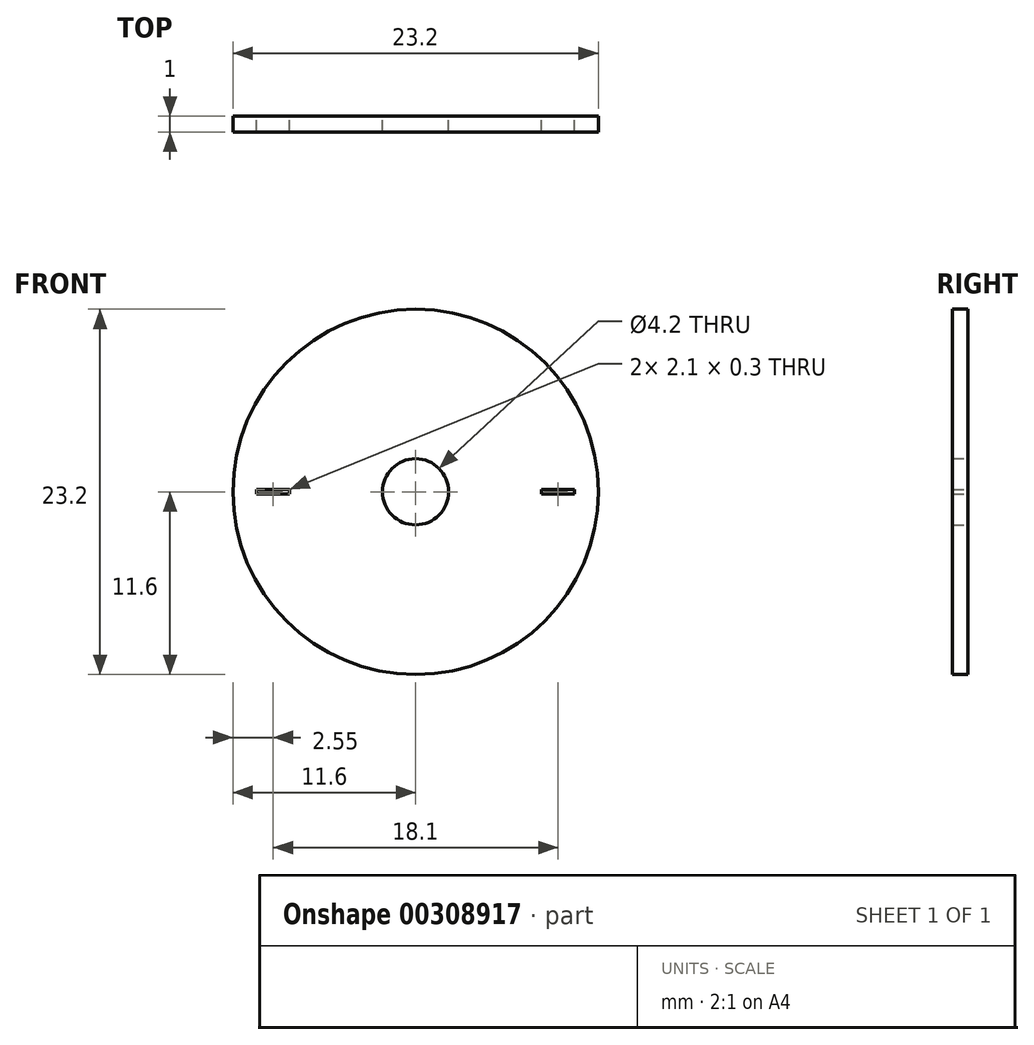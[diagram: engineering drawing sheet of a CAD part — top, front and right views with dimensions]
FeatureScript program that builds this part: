
annotation { "Feature Type Name" : "Feature", "Feature Type Description" : "" }
export const myFeature = defineFeature(function(context is Context, id is Id, definition is map)
    precondition{}
    {
        {
            var Q0;
            Q0=qCreatedBy(makeId("Front.planeOp"),FACE);
            var sketch = newSketch(context, id + "F0", { "sketchPlane" : qUnion([Q0])});
            skCircle(sketch, "E0", {"center": v(0, 0) * mm, "radius": 11.6 * mm});
            skCircle(sketch, "E1", {"center": v(0, 0) * mm, "radius": 2.1 * mm});
            skLineSegment(sketch, "E2.bottom", {"start": v(-10.1, 0.15) * mm, "end": v(-8, 0.15) * mm});
            skLineSegment(sketch, "E2.top", {"start": v(-10.1, -0.15) * mm, "end": v(-8, -0.15) * mm});
            skLineSegment(sketch, "E2.left", {"start": v(-10.1, 0.15) * mm, "end": v(-10.1, -0.15) * mm});
            skLineSegment(sketch, "E2.right", {"start": v(-8, 0.15) * mm, "end": v(-8, -0.15) * mm});
            skLineSegment(sketch, "E3", {"start": v(-9.05, 0.15) * mm, "end": v(-9.05, -0.15) * mm, "construction": true});
            skLineSegment(sketch, "E4.MirrorCS", {"start": v(8, 0.15) * mm, "end": v(8, -0.15) * mm});
            skLineSegment(sketch, "E5.MirrorCS", {"start": v(10.1, 0.15) * mm, "end": v(8, 0.15) * mm});
            skLineSegment(sketch, "E6.MirrorCS", {"start": v(10.1, -0.15) * mm, "end": v(8, -0.15) * mm});
            skLineSegment(sketch, "E7.MirrorCS", {"start": v(10.1, 0.15) * mm, "end": v(10.1, -0.15) * mm});
            skLineSegment(sketch, "E8.MirrorCS", {"start": v(9.05, 0.15) * mm, "end": v(9.05, -0.15) * mm, "construction": true});
            skSolve(sketch);
        }
        {
            var Q0;
            Q0 = qSketchRegion(id + "F0", true);
            extrude(context, id + "F1", {"entities" : qUnion([Q0]), "depth" : 1 * mm});
        }
    });
